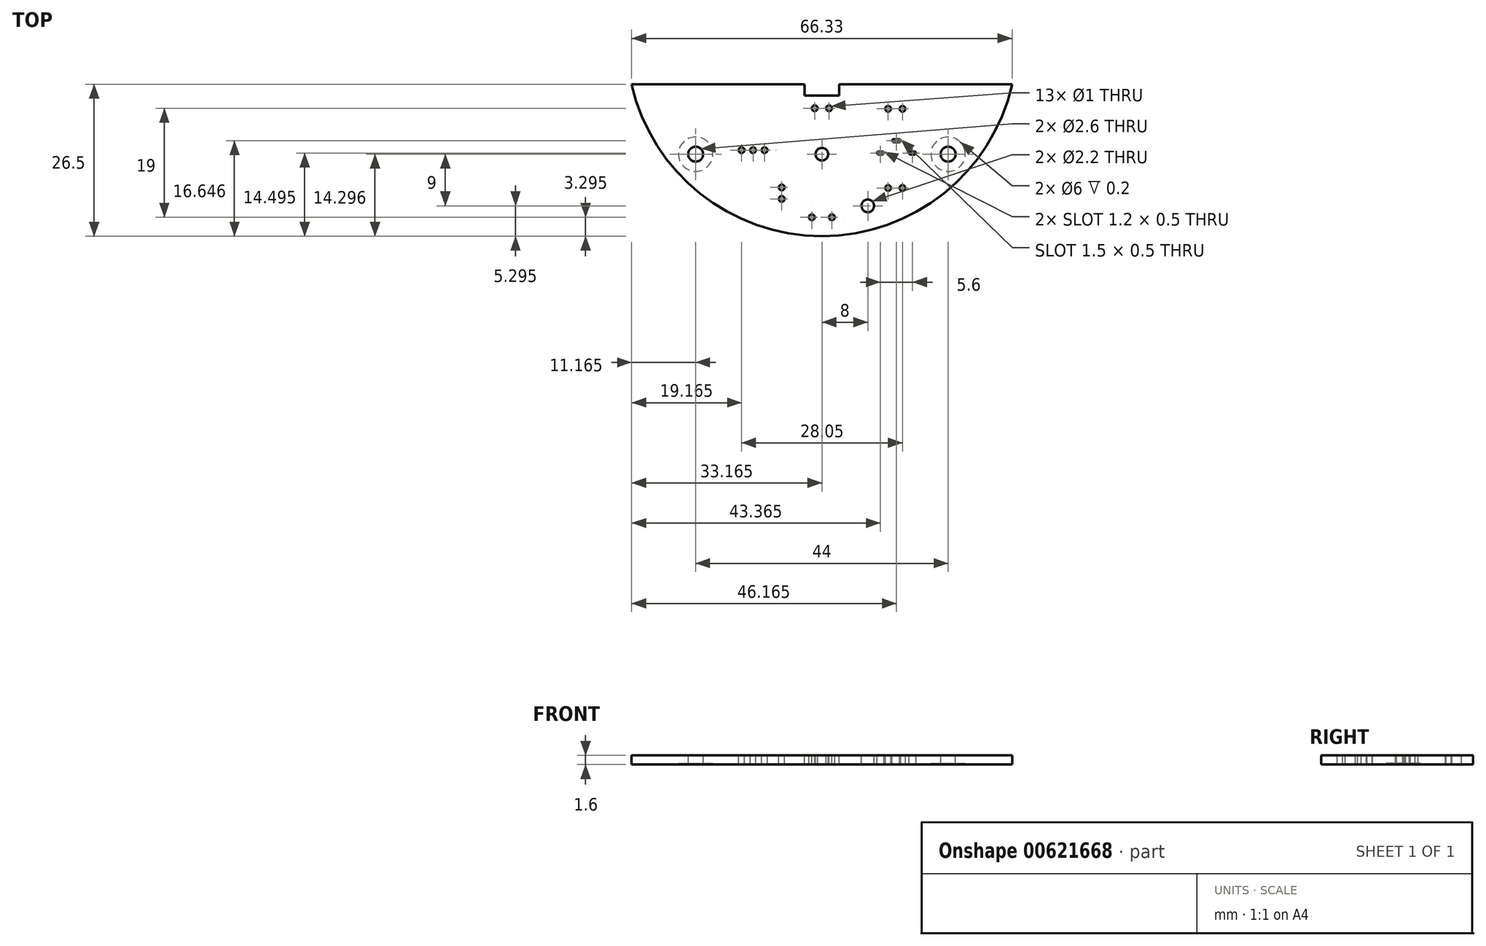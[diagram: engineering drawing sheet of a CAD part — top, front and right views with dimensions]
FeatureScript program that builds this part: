
annotation { "Feature Type Name" : "Feature", "Feature Type Description" : "" }
export const myFeature = defineFeature(function(context is Context, id is Id, definition is map)
    precondition{}
    {
        {
            var Q0;
            Q0=qCreatedBy(makeId("Top.planeOp"),FACE);
            var sketch = newSketch(context, id + "F0", { "sketchPlane" : qUnion([Q0])});
            skLineSegment(sketch, "E0.bottom", {"start": v(6.37, 29.29) * mm, "end": v(70.72, 29.29) * mm, "construction": true});
            skPoint(sketch, "E1.middle", {"position": v(38.54, 20.77) * mm});
            skPoint(sketch, "E2.orphan", {"position": v(18.04, 25.29) * mm});
            skPoint(sketch, "E3.orphan", {"position": v(59.04, 25.29) * mm});
            skArc(sketch, "E4", {"start": v(5.38, 32.79) * mm, "mid": v(38.54, 6.29) * mm, "end": v(71.7, 32.79) * mm});
            skLineSegment(sketch, "E5.0", {"start": v(5.38, 32.79) * mm, "end": v(71.7, 32.79) * mm});
            skLineSegment(sketch, "E6.0", {"start": v(5.38, 31.29) * mm, "end": v(71.7, 31.29) * mm, "construction": true});
            skSolve(sketch);
        }
        {
            var Q0;
            Q0=qSketchRegion(id+"F0",true);
            extrude(context, id + "F1", {"entities" : qUnion([Q0]), "depth" : 1.6 * mm});
        }
        {
            var Q0;
            Q0=makeQuery(id+"F1.opExtrude","CAP_FACE",FACE,{"disambiguationData":[OSD([sQuery(id+"F0.wireOp",EDGE,"E4"),sQuery(id+"F0.wireOp",EDGE,"E5.0")])],"isStart":false});
            var sketch = newSketch(context, id + "F2", { "sketchPlane" : qUnion([Q0])});
            skCircle(sketch, "E7", {"center": v(16.54, 20.59) * mm, "radius": 1.3 * mm});
            skLineSegment(sketch, "E8", {"start": v(38.54, 22.42) * mm, "end": v(38.54, 32.79) * mm, "construction": true});
            skCircle(sketch, "E9.MirrorC", {"center": v(60.54, 20.59) * mm, "radius": 1.3 * mm});
            skCircle(sketch, "E10", {"center": v(38.54, 20.59) * mm, "radius": 1.1 * mm});
            skCircle(sketch, "E11", {"center": v(46.54, 11.59) * mm, "radius": 1.1 * mm});
            skSolve(sketch);
        }
        {
            var Q0;
            Q0=qSketchRegion(id+"F2",true);
            extrude(context, id + "F3", {"entities" : qUnion([Q0]), "operationType" : NewBodyOperationType.REMOVE, "oppositeDirection" : true, "depth" : 3 * mm, "offsetDistance" : 25 * mm});
        }
        {
            var Q0;
            Q0=makeQuery(id+"F1.opExtrude","CAP_FACE",FACE,{"disambiguationData":[OSD([sQuery(id+"F0.wireOp",EDGE,"E4"),sQuery(id+"F0.wireOp",EDGE,"E5.0")])],"isStart":false});
            var sketch = newSketch(context, id + "F4", { "sketchPlane" : qUnion([Q0])});
            skCircle(sketch, "E12", {"center": v(24.54, 21.29) * mm, "radius": 0.5 * mm});
            skLineSegment(sketch, "E13", {"start": v(38.54, 22.32) * mm, "end": v(38.54, 32.79) * mm, "construction": true});
            skCircle(sketch, "E14.1.0.0", {"center": v(26.54, 21.29) * mm, "radius": 0.5 * mm});
            skLineSegment(sketch, "E14.direction1", {"start": v(24.54, 21.29) * mm, "end": v(26.54, 21.29) * mm, "construction": true});
            skCircle(sketch, "E15.0.2.0", {"center": v(28.54, 21.29) * mm, "radius": 0.5 * mm});
            skSolve(sketch);
        }
        {
            var Q0;
            Q0=makeQuery(id+"F1.opExtrude","CAP_FACE",FACE,{"disambiguationData":[OSD([sQuery(id+"F0.wireOp",EDGE,"E4"),sQuery(id+"F0.wireOp",EDGE,"E5.0")])],"isStart":false});
            var sketch = newSketch(context, id + "F5", { "sketchPlane" : qUnion([Q0])});
            skLineSegment(sketch, "E16", {"start": v(51.54, 14.1) * mm, "end": v(51.54, 27.42) * mm, "construction": true});
            skLineSegment(sketch, "E17", {"start": v(38.54, 6.29) * mm, "end": v(38.54, 24.04) * mm, "construction": true});
            skLineSegment(sketch, "E18", {"start": v(48.4, 20.79) * mm, "end": v(49.1, 20.79) * mm, "construction": true});
            skLineSegment(sketch, "E19", {"start": v(48.74, 20.79) * mm, "end": v(48.74, 23.97) * mm, "construction": true});
            skLineSegment(sketch, "E20", {"start": v(51.04, 22.94) * mm, "end": v(52.04, 22.94) * mm, "construction": true});
            skLineSegment(sketch, "E21", {"start": v(51.54, 22.94) * mm, "end": v(51.54, 19.92) * mm, "construction": true});
            skArc(sketch, "E22.0.startCap", {"start": v(51.04, 22.69) * mm, "mid": v(50.8, 22.94) * mm, "end": v(51.04, 23.19) * mm});
            skArc(sketch, "E22.0.endCap", {"start": v(52.04, 23.19) * mm, "mid": v(52.3, 22.94) * mm, "end": v(52.04, 22.69) * mm});
            skLineSegment(sketch, "E22.0.left", {"start": v(51.04, 23.19) * mm, "end": v(52.04, 23.19) * mm});
            skLineSegment(sketch, "E22.0.right", {"start": v(51.04, 22.69) * mm, "end": v(52.04, 22.69) * mm});
            skLineSegment(sketch, "E23", {"start": v(50.45, 21.94) * mm, "end": v(53.65, 21.94) * mm, "construction": true});
            skArc(sketch, "E24.0.startCap", {"start": v(49.1, 21.04) * mm, "mid": v(49.34, 20.79) * mm, "end": v(49.1, 20.54) * mm});
            skArc(sketch, "E24.0.endCap", {"start": v(48.4, 20.54) * mm, "mid": v(48.14, 20.79) * mm, "end": v(48.4, 21.04) * mm});
            skLineSegment(sketch, "E24.0.left", {"start": v(48.4, 20.54) * mm, "end": v(49.1, 20.54) * mm});
            skLineSegment(sketch, "E24.0.right", {"start": v(48.4, 21.04) * mm, "end": v(49.1, 21.04) * mm});
            skArc(sketch, "E25.MirrorCS", {"start": v(54.7, 20.54) * mm, "mid": v(54.94, 20.79) * mm, "end": v(54.7, 21.04) * mm});
            skLineSegment(sketch, "E26.MirrorCS", {"start": v(54.7, 20.54) * mm, "end": v(54, 20.54) * mm});
            skLineSegment(sketch, "E27.MirrorCS", {"start": v(54.7, 21.04) * mm, "end": v(54, 21.04) * mm});
            skArc(sketch, "E28.MirrorCS", {"start": v(54, 21.04) * mm, "mid": v(53.74, 20.79) * mm, "end": v(54, 20.54) * mm});
            skSolve(sketch);
        }
        {
            var Q0;
            Q0=makeQuery(id+"F1.opExtrude","CAP_FACE",FACE,{"disambiguationData":[OSD([sQuery(id+"F0.wireOp",EDGE,"E0.bottom"),sQuery(id+"F0.wireOp",EDGE,"E4")])],"isStart":false});
            var sketch = newSketch(context, id + "F6", { "sketchPlane" : qUnion([Q0])});
            skCircle(sketch, "E29", {"center": v(50.1, 14.69) * mm, "radius": 0.5 * mm});
            skLineSegment(sketch, "E30.direction1", {"start": v(50.1, 14.69) * mm, "end": v(52.6, 14.69) * mm, "construction": true});
            skLineSegment(sketch, "E31", {"start": v(38.54, 6.29) * mm, "end": v(38.54, 17.65) * mm, "construction": true});
            skLineSegment(sketch, "E32", {"start": v(51.34, 14.69) * mm, "end": v(51.34, 23.7) * mm, "construction": true});
            skCircle(sketch, "E33", {"center": v(52.6, 14.69) * mm, "radius": 0.5 * mm});
            skCircle(sketch, "E34", {"center": v(50.1, 28.49) * mm, "radius": 0.5 * mm});
            skCircle(sketch, "E35", {"center": v(52.6, 28.49) * mm, "radius": 0.5 * mm});
            skSolve(sketch);
        }
        {
            var Q0;
            Q0=makeQuery(id+"F1.opExtrude","CAP_FACE",FACE,{"disambiguationData":[OSD([sQuery(id+"F0.wireOp",EDGE,"E0.bottom"),sQuery(id+"F0.wireOp",EDGE,"E4")])],"isStart":false});
            var sketch = newSketch(context, id + "F7", { "sketchPlane" : qUnion([Q0])});
            skCircle(sketch, "E36", {"center": v(37.3, 28.59) * mm, "radius": 0.5 * mm});
            skCircle(sketch, "E37.1.0.0", {"center": v(39.8, 28.59) * mm, "radius": 0.5 * mm});
            skLineSegment(sketch, "E37.direction1", {"start": v(37.3, 28.59) * mm, "end": v(39.8, 28.59) * mm, "construction": true});
            skLineSegment(sketch, "E38", {"start": v(38.54, 15.29) * mm, "end": v(38.54, 32.79) * mm, "construction": true});
            skLineSegment(sketch, "E39", {"start": v(38.54, 26.14) * mm, "end": v(38.54, 28.59) * mm, "construction": true});
            skSolve(sketch);
        }
        {
            var Q0;
            Q0=makeQuery(id+"F1.opExtrude","CAP_FACE",FACE,{"disambiguationData":[OSD([sQuery(id+"F0.wireOp",EDGE,"E0.bottom"),sQuery(id+"F0.wireOp",EDGE,"E4")])],"isStart":false});
            var sketch = newSketch(context, id + "F8", { "sketchPlane" : qUnion([Q0])});
            skCircle(sketch, "E40", {"center": v(36.8, 9.59) * mm, "radius": 0.5 * mm});
            skCircle(sketch, "E41.1.0.0", {"center": v(40.3, 9.59) * mm, "radius": 0.5 * mm});
            skLineSegment(sketch, "E41.direction1", {"start": v(36.8, 9.59) * mm, "end": v(40.3, 9.59) * mm, "construction": true});
            skLineSegment(sketch, "E42", {"start": v(38.54, 32.79) * mm, "end": v(38.54, 9.59) * mm, "construction": true});
            skSolve(sketch);
        }
        {
            var Q0;
            Q0=makeQuery(id+"F1.opExtrude","CAP_FACE",FACE,{"disambiguationData":[OSD([sQuery(id+"F0.wireOp",EDGE,"E0.bottom"),sQuery(id+"F0.wireOp",EDGE,"E4")])],"isStart":false});
            var sketch = newSketch(context, id + "F9", { "sketchPlane" : qUnion([Q0])});
            skCircle(sketch, "E43", {"center": v(31.54, 12.79) * mm, "radius": 0.5 * mm});
            skCircle(sketch, "E44", {"center": v(31.54, 14.79) * mm, "radius": 0.5 * mm});
            skSolve(sketch);
        }
        {
            var Q0;
            Q0=qSketchRegion(id+"F6",true);
            var Q1;
            Q1=qSketchRegion(id+"F7",true);
            var Q2;
            Q2=qSketchRegion(id+"F8",true);
            var Q3;
            Q3=qSketchRegion(id+"F5",true);
            var Q4;
            Q4=qSketchRegion(id+"F4",true);
            var Q5;
            Q5 = qSketchRegion(id + "F9", true);
            extrude(context, id + "F10", {"entities" : qUnion([Q0, Q1, Q2, Q3, Q4, Q5]), "operationType" : NewBodyOperationType.REMOVE, "oppositeDirection" : true, "depth" : 4 * mm, "offsetDistance" : 25 * mm});
        }
        {
            var Q0;
            Q0=makeQuery(id+"F1.opExtrude","CAP_FACE",FACE,{"disambiguationData":[OSD([sQuery(id+"F0.wireOp",EDGE,"E0.bottom"),sQuery(id+"F0.wireOp",EDGE,"E4")])],"isStart":true});
            var sketch = newSketch(context, id + "F11", { "sketchPlane" : qUnion([Q0])});
            skCircle(sketch, "E45", {"center": v(60.54, -20.59) * mm, "radius": 3 * mm});
            skLineSegment(sketch, "E46", {"start": v(38.54, -32.79) * mm, "end": v(38.54, 3.6) * mm, "construction": true});
            skCircle(sketch, "E47.MirrorC", {"center": v(16.54, -20.59) * mm, "radius": 3 * mm});
            skSolve(sketch);
        }
        {
            var Q0;
            Q0=qSketchRegion(id+"F11",true);
            extrude(context, id + "F12", {"entities" : qUnion([Q0]), "operationType" : NewBodyOperationType.REMOVE, "oppositeDirection" : true, "depth" : .2 * mm});
        }
        {
            var Q0;
            Q0=makeQuery(id+"F1.opExtrude","CAP_FACE",FACE,{"disambiguationData":[OSD([sQuery(id+"F0.wireOp",EDGE,"E4"),sQuery(id+"F0.wireOp",EDGE,"E5.0")])],"isStart":false});
            var sketch = newSketch(context, id + "F13", { "sketchPlane" : qUnion([Q0])});
            skLineSegment(sketch, "E48", {"start": v(38.54, 32.79) * mm, "end": v(38.54, 37.88) * mm, "construction": true});
            skLineSegment(sketch, "E49.0", {"start": v(41.54, 32.79) * mm, "end": v(41.54, 37.88) * mm, "construction": true});
            skLineSegment(sketch, "E50.0", {"start": v(35.54, 32.79) * mm, "end": v(35.54, 37.88) * mm, "construction": true});
            skLineSegment(sketch, "E51.bottom", {"start": v(35.54, 32.79) * mm, "end": v(41.54, 32.79) * mm, "construction": true});
            skLineSegment(sketch, "E51.top", {"start": v(35.54, 32.79) * mm, "end": v(41.54, 32.79) * mm, "construction": true});
            skLineSegment(sketch, "E51.left", {"start": v(35.54, 32.79) * mm, "end": v(35.54, 32.79) * mm});
            skLineSegment(sketch, "E51.right", {"start": v(41.54, 32.79) * mm, "end": v(41.54, 32.79) * mm});
            skLineSegment(sketch, "E52.bottom", {"start": v(35.54, 32.79) * mm, "end": v(41.54, 32.79) * mm});
            skLineSegment(sketch, "E52.top", {"start": v(35.54, 30.79) * mm, "end": v(41.54, 30.79) * mm});
            skLineSegment(sketch, "E52.left", {"start": v(35.54, 32.79) * mm, "end": v(35.54, 30.79) * mm});
            skLineSegment(sketch, "E52.right", {"start": v(41.54, 32.79) * mm, "end": v(41.54, 30.79) * mm});
            skSolve(sketch);
        }
        {
            var Q0;
            Q0 = qSketchRegion(id + "F13", true);
            extrude(context, id + "F14", {"entities" : qUnion([Q0]), "operationType" : NewBodyOperationType.REMOVE, "oppositeDirection" : true, "depth" : 25 * mm, "offsetDistance" : 25 * mm});
        }
    });
